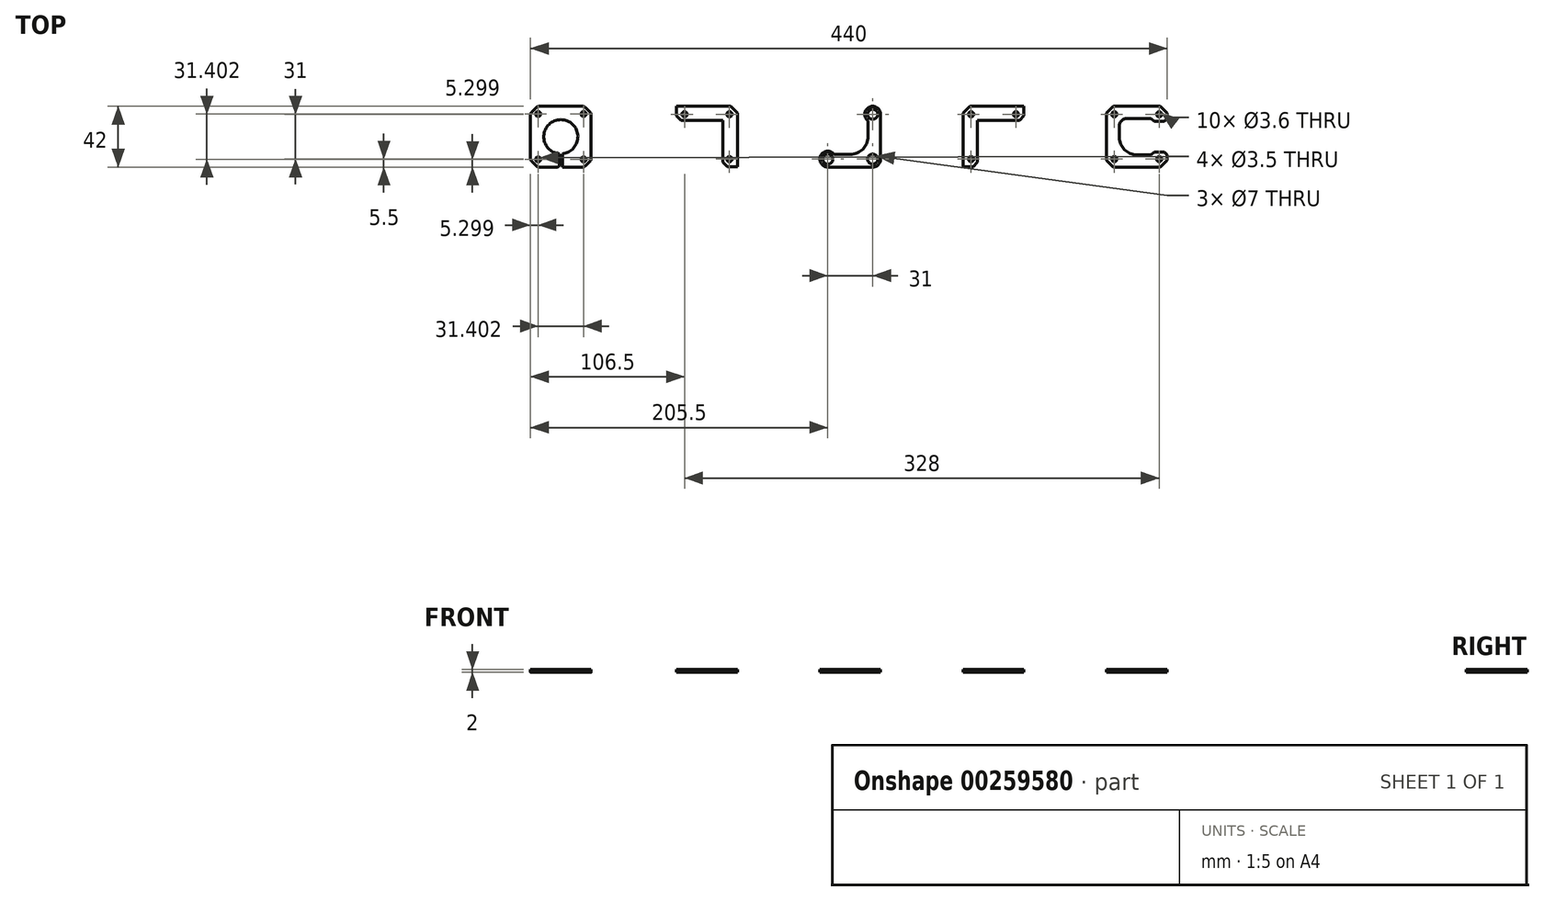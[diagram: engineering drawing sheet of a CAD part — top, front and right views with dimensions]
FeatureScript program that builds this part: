
annotation { "Feature Type Name" : "Feature", "Feature Type Description" : "" }
export const myFeature = defineFeature(function(context is Context, id is Id, definition is map)
    precondition{}
    {
        {
            var Q0;
            Q0=qCreatedBy(makeId("Top.planeOp"),FACE);
            var sketch = newSketch(context, id + "F0", { "sketchPlane" : qUnion([Q0])});
            skLineSegment(sketch, "E0.rect.bottom", {"start": v(15.5, -15.5) * mm, "end": v(-15.5, -15.5) * mm, "construction": true});
            skLineSegment(sketch, "E0.rect.top", {"start": v(15.5, 15.5) * mm, "end": v(-15.5, 15.5) * mm, "construction": true});
            skLineSegment(sketch, "E0.rect.left", {"start": v(15.5, -15.5) * mm, "end": v(15.5, 15.5) * mm, "construction": true});
            skLineSegment(sketch, "E0.rect.right", {"start": v(-15.5, -15.5) * mm, "end": v(-15.5, 15.5) * mm, "construction": true});
            skPoint(sketch, "E0.rect.middle", {"position": v(0, 0) * mm});
            skCircle(sketch, "E1", {"center": v(-15.5, -15.5) * mm, "radius": 3.5 * mm});
            skArc(sketch, "E2", {"start": v(-11.06, -12.25) * mm, "mid": v(-20.4, -13.01) * mm, "end": v(-15.5, -21) * mm});
            skCircle(sketch, "E3", {"center": v(15.5, -15.5) * mm, "radius": 3.5 * mm});
            skCircle(sketch, "E4", {"center": v(15.5, 15.5) * mm, "radius": 3.5 * mm});
            skArc(sketch, "E5", {"start": v(21, 15.5) * mm, "mid": v(13.01, 20.4) * mm, "end": v(12.25, 11.06) * mm});
            skArc(sketch, "E6", {"start": v(0, -12.25) * mm, "mid": v(8.66, -8.66) * mm, "end": v(12.25, 0) * mm});
            skLineSegment(sketch, "E7", {"start": v(0, -12.25) * mm, "end": v(-11.06, -12.25) * mm});
            skLineSegment(sketch, "E8", {"start": v(12.25, 0) * mm, "end": v(12.25, 11.06) * mm});
            skLineSegment(sketch, "E9", {"start": v(-15.5, -21) * mm, "end": v(15.5, -21) * mm});
            skLineSegment(sketch, "E10", {"start": v(21, 15.5) * mm, "end": v(21, -15.5) * mm});
            skArc(sketch, "E11", {"start": v(15.5, -21) * mm, "mid": v(19.39, -19.39) * mm, "end": v(21, -15.5) * mm});
            skLineSegment(sketch, "E12.rect.bottom", {"start": v(83.5, 15.5) * mm, "end": v(114.5, 15.5) * mm, "construction": true});
            skLineSegment(sketch, "E12.rect.top", {"start": v(83.5, -15.5) * mm, "end": v(114.5, -15.5) * mm, "construction": true});
            skLineSegment(sketch, "E12.rect.left", {"start": v(83.5, 15.5) * mm, "end": v(83.5, -15.5) * mm, "construction": true});
            skLineSegment(sketch, "E12.rect.right", {"start": v(114.5, 15.5) * mm, "end": v(114.5, -15.5) * mm, "construction": true});
            skPoint(sketch, "E12.rect.middle", {"position": v(99, 0) * mm});
            skCircle(sketch, "E13", {"center": v(83.5, -15.5) * mm, "radius": 1.8 * mm});
            skCircle(sketch, "E14", {"center": v(83.5, 15.5) * mm, "radius": 1.8 * mm});
            skCircle(sketch, "E15", {"center": v(114.5, 15.5) * mm, "radius": 1.8 * mm});
            skLineSegment(sketch, "E16", {"start": v(117, 11.3) * mm, "end": v(88, 11.3) * mm});
            skLineSegment(sketch, "E17", {"start": v(88, 11.3) * mm, "end": v(88, -17.7) * mm});
            skLineSegment(sketch, "E18", {"start": v(85, -20.7) * mm, "end": v(78, -20.7) * mm});
            skLineSegment(sketch, "E19", {"start": v(78, -20.7) * mm, "end": v(78, 16.2) * mm});
            skLineSegment(sketch, "E20", {"start": v(82.8, 21) * mm, "end": v(120, 21) * mm});
            skLineSegment(sketch, "E21", {"start": v(123, 17.3) * mm, "end": v(123, 21) * mm, "construction": true});
            skLineSegment(sketch, "E22", {"start": v(78, 16.2) * mm, "end": v(82.8, 21) * mm});
            skLineSegment(sketch, "E23", {"start": v(117, 11.3) * mm, "end": v(120, 14.3) * mm});
            skLineSegment(sketch, "E24", {"start": v(85, -20.7) * mm, "end": v(88, -17.7) * mm});
            skLineSegment(sketch, "E25", {"start": v(120, 21) * mm, "end": v(120, 14.3) * mm});
            skLineSegment(sketch, "E26", {"start": v(120, 14.3) * mm, "end": v(123, 17.3) * mm, "construction": true});
            skLineSegment(sketch, "E27", {"start": v(120, 21) * mm, "end": v(123, 21) * mm, "construction": true});
            skLineSegment(sketch, "E28.rect.bottom", {"start": v(182.5, -15.5) * mm, "end": v(213.5, -15.5) * mm, "construction": true});
            skLineSegment(sketch, "E28.rect.top", {"start": v(182.5, 15.5) * mm, "end": v(213.5, 15.5) * mm, "construction": true});
            skLineSegment(sketch, "E28.rect.left", {"start": v(182.5, -15.5) * mm, "end": v(182.5, 15.5) * mm, "construction": true});
            skLineSegment(sketch, "E28.rect.right", {"start": v(213.5, -15.5) * mm, "end": v(213.5, 15.5) * mm, "construction": true});
            skPoint(sketch, "E28.rect.middle", {"position": v(198, 0) * mm});
            skCircle(sketch, "E29", {"center": v(182.5, -15.5) * mm, "radius": 1.8 * mm});
            skCircle(sketch, "E30", {"center": v(182.5, 15.5) * mm, "radius": 1.8 * mm});
            skCircle(sketch, "E31", {"center": v(213.5, 15.5) * mm, "radius": 1.8 * mm});
            skCircle(sketch, "E32", {"center": v(213.5, -15.5) * mm, "radius": 1.8 * mm});
            skLineSegment(sketch, "E33", {"start": v(186, 7.5) * mm, "end": v(186, -0.5) * mm});
            skLineSegment(sketch, "E34.trimOffspring", {"start": v(198, -12.5) * mm, "end": v(208, -12.5) * mm});
            skPoint(sketch, "E35.visualSharp", {"position": v(186, -12.5) * mm});
            skArc(sketch, "E35.filletArc", {"start": v(186, -0.5) * mm, "mid": v(189.51, -8.99) * mm, "end": v(198, -12.5) * mm});
            skLineSegment(sketch, "E36.rect.bottom", {"start": v(177, -21) * mm, "end": v(219, -21) * mm});
            skLineSegment(sketch, "E36.rect.top", {"start": v(177, 21) * mm, "end": v(219, 21) * mm});
            skLineSegment(sketch, "E36.rect.left", {"start": v(177, -21) * mm, "end": v(177, 21) * mm});
            skLineSegment(sketch, "E36.rect.right", {"start": v(219, -21) * mm, "end": v(219, -12.5) * mm});
            skLineSegment(sketch, "E37", {"start": v(210, -10.5) * mm, "end": v(217, -10.5) * mm});
            skLineSegment(sketch, "E38", {"start": v(217, -10.5) * mm, "end": v(219, -12.5) * mm});
            skLineSegment(sketch, "E39.0.MirrorCS", {"start": v(210, -10.5) * mm, "end": v(208, -12.5) * mm});
            skLineSegment(sketch, "E40", {"start": v(198, 0) * mm, "end": v(177, 0) * mm, "construction": true});
            skLineSegment(sketch, "E41.0.MirrorCS", {"start": v(156, 0) * mm, "end": v(177, 0) * mm, "construction": true});
            skLineSegment(sketch, "E42.0.MirrorCS", {"start": v(191, 12.5) * mm, "end": v(208, 12.5) * mm});
            skLineSegment(sketch, "E43.0.MirrorCS", {"start": v(210, 10.5) * mm, "end": v(208, 12.5) * mm});
            skLineSegment(sketch, "E44.0.MirrorCS", {"start": v(210, 10.5) * mm, "end": v(217, 10.5) * mm});
            skLineSegment(sketch, "E45.0.MirrorCS", {"start": v(217, 10.5) * mm, "end": v(219, 12.5) * mm});
            skLineSegment(sketch, "E46.0.MirrorCS", {"start": v(219, 21) * mm, "end": v(219, 12.5) * mm});
            skLineSegment(sketch, "E47.rect.bottom", {"start": v(198, 37.2) * mm, "end": v(160.8, 0) * mm});
            skLineSegment(sketch, "E47.rect.top", {"start": v(235.2, 0) * mm, "end": v(198, -37.2) * mm});
            skLineSegment(sketch, "E47.rect.left", {"start": v(198, 37.2) * mm, "end": v(235.2, 0) * mm});
            skLineSegment(sketch, "E47.rect.right", {"start": v(160.8, 0) * mm, "end": v(198, -37.2) * mm});
            skPoint(sketch, "E48", {"position": v(181.8, 21) * mm});
            skPoint(sketch, "E49.visualSharp", {"position": v(186, 12.5) * mm});
            skArc(sketch, "E49.filletArc", {"start": v(191, 12.5) * mm, "mid": v(187.46, 11.04) * mm, "end": v(186, 7.5) * mm});
            skSolve(sketch);
        }
        {
            var Q0;
            Q0=makeQuery(id+"F0.imprint","IMPRINT",FACE,{"disambiguationData":[TD([[makeQuery(id+"F0.imprint","IMPRINT",EDGE,{"derivedFrom":sQuery(id+"F0.wireOp",EDGE,"E1")}),-1.0]])]});
            var Q1;
            Q1=makeQuery(id+"F0.imprint","IMPRINT",FACE,{"disambiguationData":[TD([[makeQuery(id+"F0.imprint","IMPRINT",EDGE,{"derivedFrom":sQuery(id+"F0.wireOp",EDGE,"E13")}),-1.0]])]});
            var Q2;
            Q2=makeQuery(id+"F0.imprint","IMPRINT",FACE,{"disambiguationData":[TD([[makeQuery(id+"F0.imprint","IMPRINT",EDGE,{"derivedFrom":sQuery(id+"F0.wireOp",EDGE,"E29")}),-1.0]])]});
            extrude(context, id + "F1", {"entities" : qUnion([Q0, Q1, Q2]), "depth" : 2 * mm});
        }
        {
            var Q0;
            Q0=makeQuery(id+"F1.opExtrude","SWEPT_BODY",BODY,{"disambiguationData":[OSD([sQuery(id+"F0.wireOp",EDGE,"E13"),sQuery(id+"F0.wireOp",EDGE,"E14"),sQuery(id+"F0.wireOp",EDGE,"E15"),sQuery(id+"F0.wireOp",EDGE,"E16"),sQuery(id+"F0.wireOp",EDGE,"E17"),sQuery(id+"F0.wireOp",EDGE,"E18"),sQuery(id+"F0.wireOp",EDGE,"E19"),sQuery(id+"F0.wireOp",EDGE,"E20"),sQuery(id+"F0.wireOp",EDGE,"E22"),sQuery(id+"F0.wireOp",EDGE,"E23"),sQuery(id+"F0.wireOp",EDGE,"E24"),sQuery(id+"F0.wireOp",EDGE,"E25")])]});
            var Q1;
            Q1=qCreatedBy(makeId("Right.planeOp"),FACE);
            mirror(context, id + "F2", {"entities" : qUnion([Q0]), "mirrorPlane" : qUnion([Q1])});
        }
        {
            var Q0;
            Q0=qCreatedBy(makeId("Top.planeOp"),FACE);
            var sketch = newSketch(context, id + "F3", { "sketchPlane" : qUnion([Q0])});
            skLineSegment(sketch, "E50.rect.bottom", {"start": v(14.96, -21) * mm, "end": v(0, -21) * mm});
            skLineSegment(sketch, "E50.rect.top", {"start": v(14.96, 21) * mm, "end": v(0, 21) * mm});
            skLineSegment(sketch, "E50.rect.left", {"start": v(21, -14.96) * mm, "end": v(21, 14.96) * mm});
            skLineSegment(sketch, "E51", {"start": v(17.08, 20.12) * mm, "end": v(20.12, 17.08) * mm});
            skLineSegment(sketch, "E52", {"start": v(0, 21) * mm, "end": v(0, -21) * mm, "construction": true});
            skLineSegment(sketch, "E53", {"start": v(-21, 0) * mm, "end": v(21, 0) * mm, "construction": true});
            skLineSegment(sketch, "E54.0.MirrorCS", {"start": v(17.08, -20.12) * mm, "end": v(20.12, -17.08) * mm});
            skLineSegment(sketch, "E55", {"start": v(0, 0) * mm, "end": v(21, 21) * mm, "construction": true});
            skCircle(sketch, "E56", {"center": v(15.7, 15.7) * mm, "radius": 1.75 * mm});
            skCircle(sketch, "E57.0.MirrorC", {"center": v(15.7, -15.7) * mm, "radius": 1.75 * mm});
            skArc(sketch, "E58.trimOffspring", {"start": v(0, -11.8) * mm, "mid": v(11.8, 0) * mm, "end": v(0, 11.8) * mm});
            skPoint(sketch, "E59.visualSharp", {"position": v(16.2, 21) * mm});
            skArc(sketch, "E59.filletArc", {"start": v(17.08, 20.12) * mm, "mid": v(16.1, 20.77) * mm, "end": v(14.96, 21) * mm});
            skPoint(sketch, "E60.visualSharp", {"position": v(21, 16.2) * mm});
            skArc(sketch, "E60.filletArc", {"start": v(21, 14.96) * mm, "mid": v(20.77, 16.1) * mm, "end": v(20.12, 17.08) * mm});
            skPoint(sketch, "E61.visualSharp", {"position": v(21, -16.2) * mm});
            skArc(sketch, "E61.filletArc", {"start": v(20.12, -17.08) * mm, "mid": v(20.77, -16.1) * mm, "end": v(21, -14.96) * mm});
            skPoint(sketch, "E62.visualSharp", {"position": v(16.2, -21) * mm});
            skArc(sketch, "E62.filletArc", {"start": v(14.96, -21) * mm, "mid": v(16.1, -20.77) * mm, "end": v(17.08, -20.12) * mm});
            skLineSegment(sketch, "E63", {"start": v(0, 11.8) * mm, "end": v(0, 21) * mm});
            skLineSegment(sketch, "E64", {"start": v(0, -11.8) * mm, "end": v(0, -21) * mm});
            skSolve(sketch);
        }
        {
            var Q0;
            Q0=makeQuery(id+"F3.imprint","IMPRINT",FACE,{"disambiguationData":[TD([[makeQuery(id+"F3.imprint","IMPRINT",EDGE,{"derivedFrom":sQuery(id+"F3.wireOp",EDGE,"E50.rect.bottom")}),-1.0]])]});
            extrude(context, id + "F4", {"entities" : qUnion([Q0]), "depth" : 2 * mm});
        }
        {
            var Q0;
            Q0=makeQuery(id+"F4.opExtrude","SWEPT_BODY",BODY,{"disambiguationData":[OSD([sQuery(id+"F3.wireOp",EDGE,"E50.rect.bottom"),sQuery(id+"F3.wireOp",EDGE,"E50.rect.top"),sQuery(id+"F3.wireOp",EDGE,"E50.rect.left"),sQuery(id+"F3.wireOp",EDGE,"E51"),sQuery(id+"F3.wireOp",EDGE,"E54.0.MirrorCS"),sQuery(id+"F3.wireOp",EDGE,"E56"),sQuery(id+"F3.wireOp",EDGE,"E57.0.MirrorC"),sQuery(id+"F3.wireOp",EDGE,"E58.trimOffspring"),sQuery(id+"F3.wireOp",EDGE,"E59.filletArc"),sQuery(id+"F3.wireOp",EDGE,"E60.filletArc"),sQuery(id+"F3.wireOp",EDGE,"E61.filletArc"),sQuery(id+"F3.wireOp",EDGE,"E62.filletArc"),sQuery(id+"F3.wireOp",EDGE,"E63"),sQuery(id+"F3.wireOp",EDGE,"E64")])]});
            var Q1;
            Q1=makeQuery(id+"F4.opExtrude","SWEPT_FACE",FACE,{"disambiguationData":[OSD([sQuery(id+"F3.wireOp",EDGE,"E63")])]});
            mirror(context, id + "F5", {"entities" : qUnion([Q0]), "mirrorPlane" : qUnion([Q1])});
        }
        {
            var Q0;
            Q0=makeQuery(id+"F5.opPattern","COPY",BODY,{"derivedFrom":makeQuery(id+"F4.opExtrude","SWEPT_BODY",BODY,{"disambiguationData":[OSD([sQuery(id+"F3.wireOp",EDGE,"E50.rect.bottom"),sQuery(id+"F3.wireOp",EDGE,"E50.rect.top"),sQuery(id+"F3.wireOp",EDGE,"E50.rect.left"),sQuery(id+"F3.wireOp",EDGE,"E51"),sQuery(id+"F3.wireOp",EDGE,"E54.0.MirrorCS"),sQuery(id+"F3.wireOp",EDGE,"E56"),sQuery(id+"F3.wireOp",EDGE,"E57.0.MirrorC"),sQuery(id+"F3.wireOp",EDGE,"E58.trimOffspring"),sQuery(id+"F3.wireOp",EDGE,"E59.filletArc"),sQuery(id+"F3.wireOp",EDGE,"E60.filletArc"),sQuery(id+"F3.wireOp",EDGE,"E61.filletArc"),sQuery(id+"F3.wireOp",EDGE,"E62.filletArc"),sQuery(id+"F3.wireOp",EDGE,"E63"),sQuery(id+"F3.wireOp",EDGE,"E64")])]}),"instanceName":"1"});
            var Q1;
            Q1=makeQuery(id+"F4.opExtrude","SWEPT_BODY",BODY,{"disambiguationData":[OSD([sQuery(id+"F3.wireOp",EDGE,"E50.rect.bottom"),sQuery(id+"F3.wireOp",EDGE,"E50.rect.top"),sQuery(id+"F3.wireOp",EDGE,"E50.rect.left"),sQuery(id+"F3.wireOp",EDGE,"E51"),sQuery(id+"F3.wireOp",EDGE,"E54.0.MirrorCS"),sQuery(id+"F3.wireOp",EDGE,"E56"),sQuery(id+"F3.wireOp",EDGE,"E57.0.MirrorC"),sQuery(id+"F3.wireOp",EDGE,"E58.trimOffspring"),sQuery(id+"F3.wireOp",EDGE,"E59.filletArc"),sQuery(id+"F3.wireOp",EDGE,"E60.filletArc"),sQuery(id+"F3.wireOp",EDGE,"E61.filletArc"),sQuery(id+"F3.wireOp",EDGE,"E62.filletArc"),sQuery(id+"F3.wireOp",EDGE,"E63"),sQuery(id+"F3.wireOp",EDGE,"E64")])]});
            booleanBodies(context, id + "F6", {"operationType" : BooleanOperationType.UNION, "tools" : qUnion([Q0, Q1])});
        }
        {
            var Q0;
            Q0=makeQuery(id+"F5.opPattern","COPY",BODY,{"derivedFrom":makeQuery(id+"F4.opExtrude","SWEPT_BODY",BODY,{"disambiguationData":[OSD([sQuery(id+"F3.wireOp",EDGE,"E50.rect.bottom"),sQuery(id+"F3.wireOp",EDGE,"E50.rect.top"),sQuery(id+"F3.wireOp",EDGE,"E50.rect.left"),sQuery(id+"F3.wireOp",EDGE,"E51"),sQuery(id+"F3.wireOp",EDGE,"E54.0.MirrorCS"),sQuery(id+"F3.wireOp",EDGE,"E56"),sQuery(id+"F3.wireOp",EDGE,"E57.0.MirrorC"),sQuery(id+"F3.wireOp",EDGE,"E58.trimOffspring"),sQuery(id+"F3.wireOp",EDGE,"E59.filletArc"),sQuery(id+"F3.wireOp",EDGE,"E60.filletArc"),sQuery(id+"F3.wireOp",EDGE,"E61.filletArc"),sQuery(id+"F3.wireOp",EDGE,"E62.filletArc"),sQuery(id+"F3.wireOp",EDGE,"E63"),sQuery(id+"F3.wireOp",EDGE,"E64")])]}),"instanceName":"1"});
            transform(context, id + "F7", {"entities" : qUnion([Q0]), "transformType" : TransformType.TRANSLATION_3D, "dx" : -200 * mm, "dy" : 0 * mm, "dz" : 0 * mm, "makeCopy" : false});
        }
        {
            var Q0;
            {var subQ0=makeQuery(id+"F4.opExtrude","CAP_FACE",FACE,{"disambiguationData":[OSD([sQuery(id+"F3.wireOp",EDGE,"E50.rect.bottom"),sQuery(id+"F3.wireOp",EDGE,"E50.rect.top"),sQuery(id+"F3.wireOp",EDGE,"E50.rect.left"),sQuery(id+"F3.wireOp",EDGE,"E51"),sQuery(id+"F3.wireOp",EDGE,"E54.0.MirrorCS"),sQuery(id+"F3.wireOp",EDGE,"E56"),sQuery(id+"F3.wireOp",EDGE,"E57.0.MirrorC"),sQuery(id+"F3.wireOp",EDGE,"E58.trimOffspring"),sQuery(id+"F3.wireOp",EDGE,"E59.filletArc"),sQuery(id+"F3.wireOp",EDGE,"E60.filletArc"),sQuery(id+"F3.wireOp",EDGE,"E61.filletArc"),sQuery(id+"F3.wireOp",EDGE,"E62.filletArc"),sQuery(id+"F3.wireOp",EDGE,"E63"),sQuery(id+"F3.wireOp",EDGE,"E64")])],"isStart":false});Q0=makeQuery(id+"F6.opBoolean","MERGE",FACE,{"derivedFrom":[subQ0,makeQuery(id+"F5.opPattern","COPY",FACE,{"derivedFrom":subQ0,"instanceName":"1"})]});}
            var sketch = newSketch(context, id + "F8", { "sketchPlane" : qUnion([Q0])});
            skCircle(sketch, "E65.0", {"center": v(-200, 0) * mm, "radius": 11.8 * mm});
            skLineSegment(sketch, "E66.0", {"start": v(-214.96, -21) * mm, "end": v(-185.04, -21) * mm});
            skLineSegment(sketch, "E67", {"start": v(-200, -21) * mm, "end": v(-200, -11.8) * mm, "construction": true});
            skLineSegment(sketch, "E68.0", {"start": v(-199, -21) * mm, "end": v(-199, -11.76) * mm});
            skLineSegment(sketch, "E69.MirrorCS", {"start": v(-201, -21) * mm, "end": v(-201, -11.76) * mm});
            skSolve(sketch);
        }
        {
            var Q0;
            {var subQ0=sQuery(id+"F8.wireOp",EDGE,"E68.0");Q0=makeQuery(id+"F8.imprint","IMPRINT",FACE,{"disambiguationData":[TD([[makeQuery(id+"F8.imprint","IMPRINT",EDGE,{"derivedFrom":subQ0}),1.0]])]});}
            extrude(context, id + "F9", {"entities" : qUnion([Q0]), "operationType" : NewBodyOperationType.REMOVE, "oppositeDirection" : true, "depth" : 25 * mm});
        }
        {
            var Q0;
            Q0=makeQuery(id+"F9.boolean.opBoolean","COPY",EDGE,{"derivedFrom":makeQuery(id+"F9.opExtrude","SWEPT_EDGE",EDGE,{"disambiguationData":[OSD([sQuery(id+"F8.wireOp",EDGE,"E66.0"),sQuery(id+"F8.wireOp",EDGE,"E68.0")])]})});
            var Q1;
            Q1=makeQuery(id+"F9.boolean.opBoolean","COPY",EDGE,{"derivedFrom":makeQuery(id+"F9.opExtrude","SWEPT_EDGE",EDGE,{"disambiguationData":[OSD([sQuery(id+"F8.wireOp",EDGE,"E66.0"),sQuery(id+"F8.wireOp",EDGE,"E69.MirrorCS")])]})});
            var Q2;
            Q2=makeQuery(id+"F9.boolean.opBoolean","COPY",EDGE,{"derivedFrom":makeQuery(id+"F9.opExtrude","SWEPT_EDGE",EDGE,{"disambiguationData":[OSD([sQuery(id+"F8.wireOp",EDGE,"E65.0"),sQuery(id+"F8.wireOp",EDGE,"E69.MirrorCS")])]})});
            var Q3;
            Q3=makeQuery(id+"F9.boolean.opBoolean","COPY",EDGE,{"derivedFrom":makeQuery(id+"F9.opExtrude","SWEPT_EDGE",EDGE,{"disambiguationData":[OSD([sQuery(id+"F8.wireOp",EDGE,"E65.0"),sQuery(id+"F8.wireOp",EDGE,"E68.0")])]})});
            fillet(context, id + "F10", {"entities" : qUnion([Q0, Q1, Q2, Q3]), "radius" : 1.5 * mm, "tangentPropagation" : true, "allowEdgeOverflow" : false});
        }
    });
